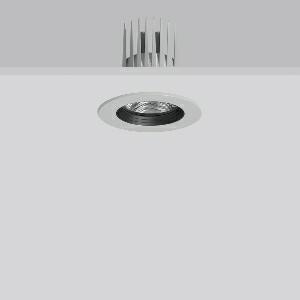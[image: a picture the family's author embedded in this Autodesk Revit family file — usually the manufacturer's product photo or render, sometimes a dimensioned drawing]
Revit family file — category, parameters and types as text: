
# Revit family: heledon_mini_e_901740_004_3_76_c245
name_source: partatom
category: Lighting Fixtures
units: mm (PartAtom-declared; Revit-internal decimal feet)

## family parameters
Cut with Voids When Loaded = No
Host = Face
Light Source = No
Part Type = Normal
Room Calculation Point = No
Round Connector Dimension = Use Diameter
Shared = No

## types (1)
- HELEDON mini E (1 x LED Modul 935, 2600 lm, 3500)
    Apparent Load = 20 VA
    Approval mark = CE
    CIE Flux Codes = 100 100 100 100 100
    Color Rendering = 92
    Color Temperature = 3500
    Default Elevation = 1800 mm
    Description = Series: HELEDON mini
Round recessed downlight. Housing: die-cast aluminium, powder-coated. Black plastic ring and recessed LED to prevent glare from the side. Optical assembly with reflector made of MIRO-Silver with 98% total light reflection for outstanding efficiency - can be changed without tools. Best colour rendering index Ra>90. Suitable for Recessed ceiling mounting. Installation without tools thanks to spring fastening system. Including separate LED converter with connecting cable 600 mm.High quality converter without flickering and stroboscopic effect. Through-wiring box (5 pole) available as accessory. The following accessories can be mounted without use of tools: interchangeable lenses, decorative glasses, honeycomb louvre, clear and frosted diffusers, white interchangeable plastic ring. 
Colour: silver
Diameter: 124 mm
Height: 3 mm
Cut-out diameter: 114 mm
Recess height: 170 mm
Luminaire: recess height: 120 mm
Lamp: LED
Socket: without socket
Colour temperature: 3500K
Colour rendering index (CRI): 92
System power: 20 W
Rated luminous flux: 2600 lm
Luminous efficiency: 130 lm/W
Control gear: Converter, dimmable, DALI
Protection class: II
Type of protection: IP 20
    Height = 0 mm  [stored 0 ft]
    Lamp = 1 x LED Modul 935
    Lamp Light Flux = 2600 lm
    Lamp count = 1
    Length = 124 mm  [stored 0.406824 ft]
    Lifetime = 50000 h
    Luminous efficacy = 130 lm/W
    Manufacturer = RZB
    ModVariant = No
    Model = 901740.004.3.76
    Mounting Place = Ceiling
    Mounting Type = Recessed
    Number of Poles = 1
    OnlyDefault = Yes
    Power Factor = 1
    Product Name = HELEDON mini E
    Product group = Recessed downlights
    ProductGroupID = 402
    Protection Class = Protection class II
    Protection Degree = IP 20
    RLX_Detail_Level = 1
    RLX_Emergency_Light_Flux = 0 lm
    RLX_Emergency_Type = 0
    RLX_Emergency_Type_DB = No
    RlxData = <blob elided: 127569 chars, md5=58e5c794>
    Socket = socket
    Standby Power = 0 W
    System Light Flux = 2600 lm
    System Power = 20 W
    Type Comments = Product without accessories
    Type Image = 901657.004.jpg
    URL = http://relux.com
    VarID = ---
    Voltage = 230 V
    Voltage Range = 220-240 V
    Weight = 0.00 kg
    Width = 0 mm  [stored 0 ft]

note: [stored X ft] marks values corroborated as IEEE doubles in the binary element streams (Revit-internal decimal feet)

## geometry (parser evidence)
native form markers: Blend x4, Sweep x13
no freeform markers — native parametric forms only
